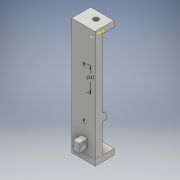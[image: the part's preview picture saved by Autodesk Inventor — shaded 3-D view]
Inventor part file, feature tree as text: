
AUTODESK INVENTOR PART (.ipt)
format: ipt  version: 2018 (Build 220112000, 112)  size: 618,496 bytes
history: native  units: mm
features: sketch x40, extrude x27, hole x8, fillet x5
ambient origin geometry x8: Origin, YZ Plane, XZ Plane, XY Plane, X Axis, Y Axis, Z Axis, Center Point
bodies: Solid1 (feature_tree)
feature tree (80):
  extrude  "Extrusion1"  Depth=100.0mm
  extrude  "Extrusion2"  Depth=5.0mm
  sketch  "Sketch3"  dims[d5=5.0mm d6=40.0mm d7=0.0mm]
  hole  "Hole1"  [1 undecoded]
  extrude  "Extrusion3"  Depth=2.0mm
  hole  "Hole2"  [1 undecoded]
  fillet  "Fillet1"  Radius=8.5mm
  extrude  "Extrusion4"  TaperAngle=90.0deg  [1 undecoded]
  extrude  "Extrusion5"  TaperAngle=180.0deg  [1 undecoded]
  hole  "Hole3"  [1 undecoded]
  fillet  "Fillet2"  Radius=3.5mm
  extrude  "Extrusion6"  Depth=10.0mm
  extrude  "Extrusion7"  Depth=5.0mm TaperAngle=0.0deg
  extrude  "Extrusion8"  Depth=12.5mm TaperAngle=0.0deg
  extrude  "Extrusion9"  Depth=0.1mm
  hole  "Hole4"  [1 undecoded]
  extrude  "Extrusion10"  Depth=5.5mm
  hole  "Hole5"  [1 undecoded]
  extrude  "Extrusion11"  Depth=2.1mm TaperAngle=0.0deg
  extrude  "Extrusion12"  Depth=5.0mm
  extrude  "Extrusion13"  Depth=1.0mm TaperAngle=0.0deg
  extrude  "Extrusion14"  Depth=3.8mm TaperAngle=0.0deg
  sketch  "Sketch21"  dims[d66=6.35mm d67=3.8mm d68=0.0mm]
  extrude  "Extrusion15"  Depth=8.0mm TaperAngle=0.0deg
  sketch  "Sketch23"  dims[d78=3.3mm d79=6.0mm d80=4.0mm d81=2.0mm d82=90.0deg d83=80.0mm d84=20.594885mm d85=5.45mm]
  extrude  "Extrusion16"  Depth=2.0mm
  extrude  "Extrusion17"  Depth=10.5mm
  hole  "Hole6"  [1 undecoded]
  fillet  "Fillet3"  Radius=4.5mm
  extrude  "Extrusion18"  Depth=8.0mm TaperAngle=0.0deg
  sketch  "Sketch28"  dims[d100=4.1mm d101=0.0mm d102=5.0mm]
  extrude  "Extrusion19"  Depth=10.0mm
  extrude  "Extrusion20"  Depth=5.0mm
  extrude  "Extrusion21"  Depth=10.0mm TaperAngle=0.0deg
  hole  "Hole7"  [1 undecoded]
  extrude  "Extrusion22"  Depth=21.0mm
  extrude  "Extrusion23"  Depth=7.499983mm TaperAngle=0.0deg
  fillet  "Fillet4"  Radius=50.0mm
  fillet  "Fillet5"  Radius=7.499983mm
  extrude  "Extrusion24"  Depth=10.0mm
  extrude  "Extrusion25"  Depth=4.1mm TaperAngle=0.0deg
  hole  "Hole8"  [1 undecoded]
  extrude  "Extrusion26"  Depth=8.0mm TaperAngle=0.0deg
  sketch  "Sketch39"  dims[d142=3.85mm d143=0.0mm]
  extrude  "Extrusion27"  Depth=1.0mm
  sketch  "Sketch1"  dims[d0=22.65mm d1=100.0mm]
  sketch  "Sketch2"  dims[d2=5.0mm d3=0.0mm d4=5.0mm]
  sketch  "Sketch4"  dims[d8=10.0mm]
  sketch  "Sketch5"  dims[d9=4.0mm d10=6.0mm d11=4.0mm d12=2.0mm d13=90.0deg d14=115.0mm d15=20.594885mm d16=23.0mm]
  sketch  "Sketch6"  dims[d17=102.75mm d18=0.0mm d19=1.175mm d20=8.5mm]
  sketch  "Sketch7"  dims[d21=21.0mm d22=90.0deg]
  sketch  "Sketch8"  dims[d23=8.5mm d24=180.0deg]
  sketch  "Sketch9"  dims[d25=21.0mm]
  sketch  "Sketch10"  dims[d26=4.0mm d27=6.0mm d28=4.0mm d29=2.0mm d30=90.0deg d31=115.0mm d32=20.594885mm d33=1.0mm d34=3.5mm]
  sketch  "Sketch11"  dims[d35=15.825mm d36=10.0mm]
  sketch  "Sketch12"  dims[d37=10.0mm d38=5.0mm d39=0.0mm]
  sketch  "Sketch13"  dims[d40=5.0mm d41=12.5mm d42=0.0mm]
  sketch  "Sketch14"  dims[d43=6.0mm d44=6.0mm d45=4.0mm d46=2.0mm d47=90.0deg d48=115.0mm d49=20.594885mm d50=0.1mm]
  sketch  "Sketch15"  dims[d51=4.25mm d52=1000.0mm d53=0.0mm]
  sketch  "Sketch16"  dims[d54=3.3mm d55=5.5mm]
  sketch  "Sketch17"  dims[d56=3.2mm d57=3.0mm]
  sketch  "Sketch18"  dims[d58=2.1mm d59=91.25mm d60=0.0mm]
  sketch  "Sketch19"  dims[d61=4.44mm d62=5.0mm]
  sketch  "Sketch20"  dims[d63=1.0mm d64=91.25mm d65=0.0mm]
  sketch  "Sketch22"  dims[d69=3.3mm d70=6.0mm d71=4.0mm d72=2.0mm d73=90.0deg d74=8.0mm d75=20.594885mm d76=4.55mm d77=0.0mm]
  sketch  "Sketch24"  dims[d86=129.8mm d87=0.0mm d88=10.5mm]
  sketch  "Sketch25"  dims[d89=2.5mm d90=0.0mm d91=10.0mm d92=4.5mm d93=0.0mm]
  sketch  "Sketch26"  dims[d94=8.0mm d95=0.0mm d96=15.5mm d97=0.0mm]
  sketch  "Sketch27"  dims[d98=10.0mm d99=10.0mm]
  sketch  "Sketch29"  dims[d103=17.5mm d104=10.0mm d105=0.0mm]
  sketch  "Sketch30"  dims[d106=5.0mm]
  sketch  "Sketch31"  dims[d107=6.0mm d108=6.0mm d109=4.0mm d110=2.0mm d111=90.0deg d112=80.0mm d113=20.594885mm d114=2.0mm]
  sketch  "Sketch32"  dims[d115=45.0mm d116=0.0mm d117=21.0mm]
  sketch  "Sketch33"  dims[d118=4.5mm d119=118.0mm d120=0.0mm d121=50.0mm d122=7.499983mm]
  sketch  "Sketch34"  dims[d123=7.5mm d124=10.0mm]
  sketch  "Sketch35"  dims[d125=10.0mm d126=4.1mm d127=0.0mm]
  sketch  "Sketch36"  dims[d128=13.4mm d129=0.0mm d130=5.0mm]
  sketch  "Sketch37"  dims[d131=6.0mm d132=6.0mm d133=4.0mm d134=2.0mm d135=90.0deg d136=8.0mm d137=20.594885mm d138=130.4mm d139=0.0mm]
  sketch  "Sketch38"  dims[d140=1.0mm d141=1.0mm]
  sketch  "Sketch40"  dims[d144=3.0mm d145=2.0mm d146=100.0mm d147=0.0mm d148=4.0mm d149=10.0mm d150=5.0mm d151=15.0mm d152=7.5mm d153=7.5mm d154=0.0mm d155=6.0mm d156=6.0mm d157=4.0mm d158=2.0mm d159=90.0deg d160=8.0mm d161=20.594885mm d162=5.5mm d163=5.0mm d164=0.0mm d165=5.5mm d166=0.0mm]
note: 10 required parameter values undecoded (feature->parameter linkage not recoverable at this tier; creation-order binding heuristic only, values carry confidence <= 0.55)
